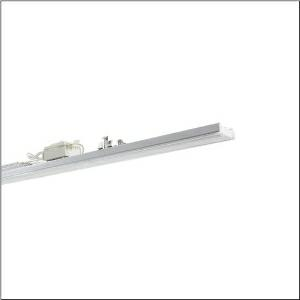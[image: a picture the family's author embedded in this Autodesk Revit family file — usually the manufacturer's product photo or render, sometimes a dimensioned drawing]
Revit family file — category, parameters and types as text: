
# Revit family: licross_r__21_recessed_mo_52tl12dv4fxg3s_6da0
name_source: partatom
category: Lighting Fixtures
units: mm (PartAtom-declared; Revit-internal decimal feet)

## family parameters
Cut with Voids When Loaded = No
Host = Face
Light Source = No
Part Type = Normal
Room Calculation Point = No
Round Connector Dimension = Use Diameter
Shared = No

## types (1)
- --- (1 x LED, 950 lm, 5.5 W, 4000K)
    Apparent Load = 6 VA
    CIE Flux Codes = 72 92 99 100 100
    Color Rendering = 80
    Color Temperature = 4000K
    Default Elevation = 1800 mm
    Description = Licross® 21 Recessed MO, luminaire insert, of sheet steel, galvanised, coil coated, white, length: 2.250mm, width: 66mm, height: 67mm, LED rated luminous flux: 15.420lm, light colour: 840, control gear: DALI 2 (for two DALI lines), with plug, 6-pole, with phase selection, for trunking rail, 14-core, mains connection: 220..240V, AC, 50/60Hz, rated input power: 89W, for trunking rail, 14-core, halogen-free wiring, for emergency light function, converter,control gear: single battery element, battery: LiFePO4, 9Ah, primary optical cover: cover, of PMMA, light emission: direct distribution, primary light characteristic: symmetric, protection rating (complete): IP40, insulation class (complete): insulation class I (protective earthing), certification: CE, UKCA, protection symbol: D if used in an environment without relevant dust loads with corresponding accessories, impact resistance: IK06, permissible ambient temperature for indoor applications: +5..+35°C, standard: EN 60598-2-22, LABS conformity tested according to VDMA 24364:2018-05, reducing of maximum allowable ambient temperature of 5°C with ceiling mounting, corresponds to IFS (International Featured Standards) requirements for safety and quality in the food industry, packaging unit: 1 piece
    Height = 58 mm
    Lamp = 1 x LED
    Lamp Light Flux = 950 lm
    Lamp Power = 5.5 W
    Lamp count = 1
    Length = 2250 mm
    Luminous efficacy = 173 lm/W
    Manufacturer = Siteco
    ModVariant = No
    Model = 52TL12DV4FXG3S
    Mounting Place = Ceiling
    Mounting Type = Pendant
    Number of Poles = 1
    OnlyDefault = Yes
    Power Factor = 1
    Product Name = Licross® 21 Recessed MO
    Product group = luminaire insert
    ProductGroupID = 902
    Protection Class = Protection class I
    Protection Degree = IP 40
    RLX_Detail_Level = 1
    RLX_Emergency_Light_Flux = 0 lm
    RLX_Emergency_Type = 0
    RLX_Emergency_Type_DB = No
    RlxData = <blob elided: 30205 chars, md5=d51fde17>
    Socket = socket
    Standby Power = 0 W
    System Light Flux = 950 lm
    System Power = 6 W
    Type Comments = : emergency light operation: 3 h
    Type Image = l_1296930.jpg
    URL = http://relux.com
    VarID = @adj_110072
    Voltage = 0 V
    Weight = 0.00 kg
    Width = 66 mm

## geometry (parser evidence)
native form markers: Blend x4, Sweep x9
no freeform markers — native parametric forms only
